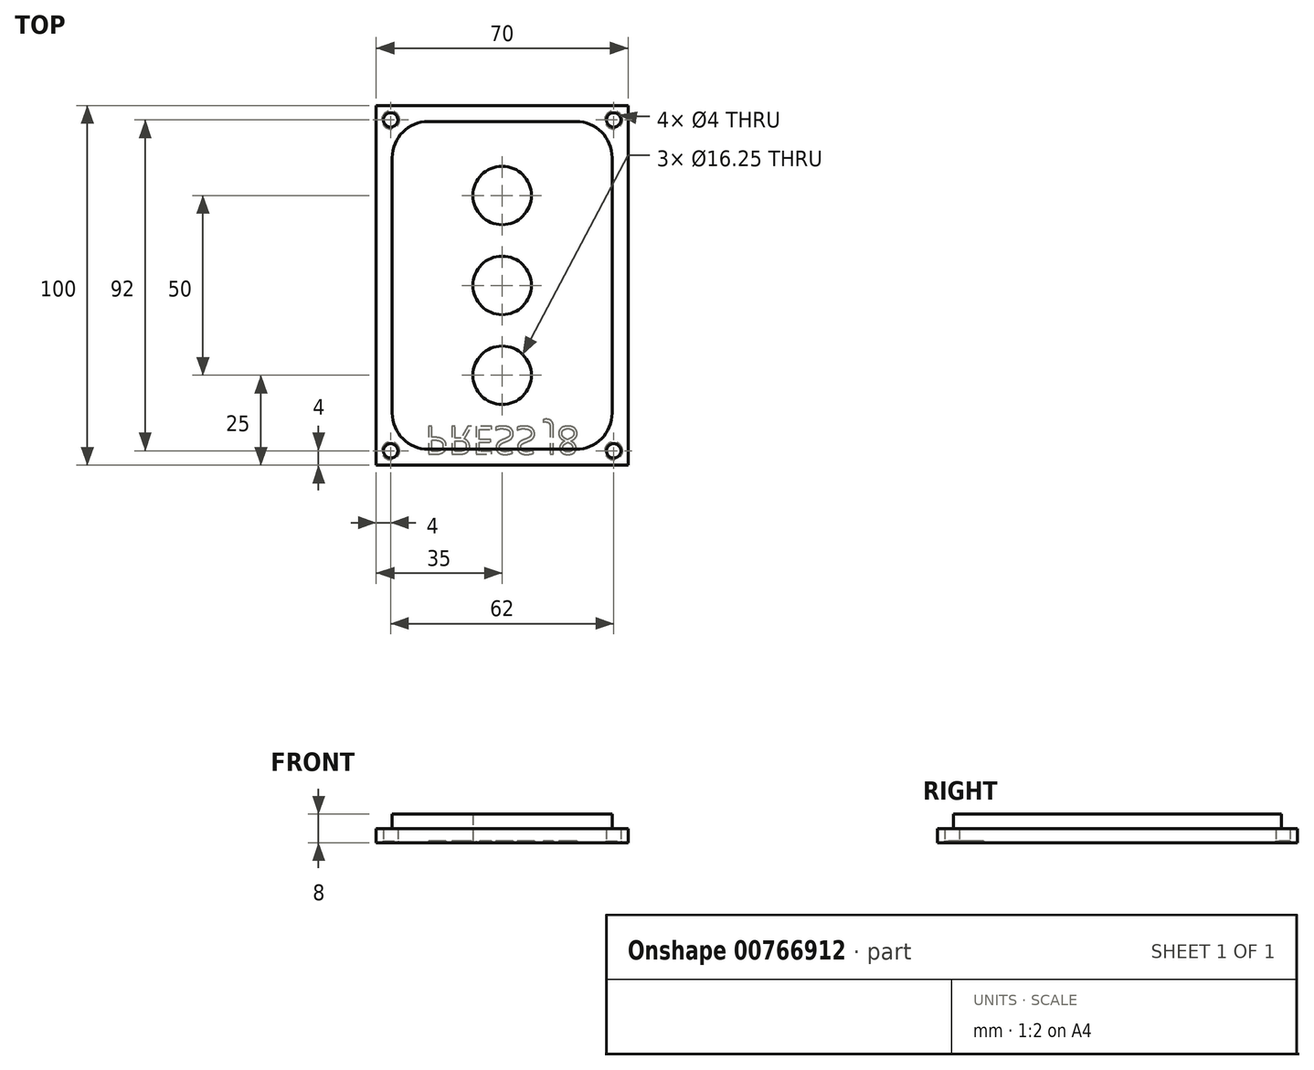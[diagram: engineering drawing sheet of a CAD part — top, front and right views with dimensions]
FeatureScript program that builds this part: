
annotation { "Feature Type Name" : "Feature", "Feature Type Description" : "" }
export const myFeature = defineFeature(function(context is Context, id is Id, definition is map)
    precondition{}
    {
        {
            var Q0;
            Q0=qCreatedBy(makeId("Top.planeOp"),FACE);
            var sketch = newSketch(context, id + "F0", { "sketchPlane" : qUnion([Q0])});
            skLineSegment(sketch, "E0.bottom", {"start": v(-35, 50) * mm, "end": v(35, 50) * mm});
            skLineSegment(sketch, "E0.top", {"start": v(-35, -50) * mm, "end": v(35, -50) * mm});
            skLineSegment(sketch, "E0.left", {"start": v(-35, 50) * mm, "end": v(-35, -50) * mm});
            skLineSegment(sketch, "E0.right", {"start": v(35, 50) * mm, "end": v(35, -50) * mm});
            skSolve(sketch);
        }
        {
            var Q0;
            Q0=qCreatedBy(makeId("Top.planeOp"),FACE);
            var sketch = newSketch(context, id + "F1", { "sketchPlane" : qUnion([Q0])});
            skLineSegment(sketch, "E1.bottom", {"start": v(-30.55, 45.55) * mm, "end": v(30.55, 45.55) * mm});
            skLineSegment(sketch, "E1.top", {"start": v(-30.55, -45.55) * mm, "end": v(30.55, -45.55) * mm});
            skLineSegment(sketch, "E1.left", {"start": v(-30.55, 45.55) * mm, "end": v(-30.55, -45.55) * mm});
            skLineSegment(sketch, "E1.right", {"start": v(30.55, 45.55) * mm, "end": v(30.55, -45.55) * mm});
            skSolve(sketch);
        }
        {
            var Q0;
            Q0=makeQuery(id+"F0.imprint","IMPRINT",FACE,{"disambiguationData":[TD([[makeQuery(id+"F0.imprint","IMPRINT",EDGE,{"derivedFrom":sQuery(id+"F0.wireOp",EDGE,"E0.bottom")}),-1.0]])]});
            extrude(context, id + "F2", {"entities" : qUnion([Q0]), "oppositeDirection" : true, "depth" : 4 * mm, "offsetDistance" : 25 * mm});
        }
        {
            var Q0;
            Q0=makeQuery(id+"F1.imprint","IMPRINT",FACE,{"disambiguationData":[TD([[makeQuery(id+"F1.imprint","IMPRINT",EDGE,{"derivedFrom":sQuery(id+"F1.wireOp",EDGE,"E1.bottom")}),-1.0]])]});
            extrude(context, id + "F3", {"entities" : qUnion([Q0]), "operationType" : NewBodyOperationType.ADD, "depth" : 4 * mm, "offsetDistance" : 25 * mm});
        }
        {
            var Q0;
            Q0=makeQuery(id+"F2.opExtrude","CAP_FACE",FACE,{"disambiguationData":[OSD([sQuery(id+"F0.wireOp",EDGE,"E0.bottom"),sQuery(id+"F0.wireOp",EDGE,"E0.top"),sQuery(id+"F0.wireOp",EDGE,"E0.left"),sQuery(id+"F0.wireOp",EDGE,"E0.right")])],"isStart":false});
            var sketch = newSketch(context, id + "F4", { "sketchPlane" : qUnion([Q0])});
            skPoint(sketch, "E2", {"position": v(0, 25) * mm});
            skPoint(sketch, "E3", {"position": v(0, 0) * mm});
            skPoint(sketch, "E4", {"position": v(0, -25) * mm});
            skSolve(sketch);
        }
        {
            var Q0;
            Q0=sQuery(id+"F4.wireOp",VERTEX,"E2");
            var Q1;
            Q1=sQuery(id+"F4.wireOp",VERTEX,"E3");
            var Q2;
            Q2=sQuery(id+"F4.wireOp",VERTEX,"E4");
            var Q3;
            Q3=makeQuery(id+"F2.opExtrude","SWEPT_BODY",BODY,{"disambiguationData":[OSD([sQuery(id+"F0.wireOp",EDGE,"E0.bottom"),sQuery(id+"F0.wireOp",EDGE,"E0.top"),sQuery(id+"F0.wireOp",EDGE,"E0.left"),sQuery(id+"F0.wireOp",EDGE,"E0.right")])]});
            hole(context, id + "F5", {"style" : HoleStyle.SIMPLE, "endStyle" : HoleEndStyle.BLIND, "holeDiameter" : 16.25 * mm, "majorDiameter" : 5 * mm, "holeDepth" : 10 * mm, "isTappedThrough" : true, "tappedDepth" : 12 * mm, "tapClearance" : 3, "locations" : qUnion([Q0, Q1, Q2]), "scope" : qUnion([Q3])});
        }
        {
            var Q0;
            Q0=makeQuery(id+"F2.opExtrude","CAP_FACE",FACE,{"disambiguationData":[OSD([sQuery(id+"F0.wireOp",EDGE,"E0.bottom"),sQuery(id+"F0.wireOp",EDGE,"E0.top"),sQuery(id+"F0.wireOp",EDGE,"E0.left"),sQuery(id+"F0.wireOp",EDGE,"E0.right")])],"isStart":false});
            var sketch = newSketch(context, id + "F6", { "sketchPlane" : qUnion([Q0])});
            skText(sketch, "E5", { "text": "PRESS J8", "fontName": "OpenSans-Regular.ttf"});
            const initialGuessF6  = {"E5": [-0.0215, 0.03923, 1, 0, 0.00777]};
            skSetInitialGuess(sketch, initialGuessF6);
            skSolve(sketch);
        }
        {
            var Q0;
            Q0 = qSketchRegion(id + "F6", true);
            extrude(context, id + "F7", {"entities" : qUnion([Q0]), "operationType" : NewBodyOperationType.REMOVE, "oppositeDirection" : true, "depth" : .5 * mm, "offsetDistance" : 25 * mm});
        }
        {
            var Q0;
            {var subQ0=sQuery(id+"F0.wireOp",EDGE,"E0.top");var subQ1=sQuery(id+"F0.wireOp",EDGE,"E0.right");var subQ2=sQuery(id+"F0.wireOp",EDGE,"E0.left");var subQ3=sQuery(id+"F0.wireOp",EDGE,"E0.bottom");Q0=makeQuery(id+"F7.boolean.opBoolean","SPLIT",FACE,{"disambiguationData":[TD([makeQuery(id+"F2.opExtrude","SWEPT_FACE",FACE,{"disambiguationData":[OSD([subQ3])]})])],"derivedFrom":makeQuery(id+"F2.opExtrude","CAP_FACE",FACE,{"disambiguationData":[OSD([subQ3,subQ0,subQ2,subQ1])],"isStart":false})});}
            var sketch = newSketch(context, id + "F8", { "sketchPlane" : qUnion([Q0])});
            skPoint(sketch, "E6", {"position": v(-31, 46) * mm});
            skPoint(sketch, "E7", {"position": v(31, 46) * mm});
            skPoint(sketch, "E8", {"position": v(31, -46) * mm});
            skPoint(sketch, "E9", {"position": v(-31, -46) * mm});
            skSolve(sketch);
        }
        {
            var Q0;
            Q0=makeQuery(id+"F3.opExtrude","SWEPT_EDGE",EDGE,{"disambiguationData":[OSD([sQuery(id+"F1.wireOp",EDGE,"E1.top"),sQuery(id+"F1.wireOp",EDGE,"E1.left")])]});
            var Q1;
            Q1=makeQuery(id+"F3.opExtrude","SWEPT_EDGE",EDGE,{"disambiguationData":[OSD([sQuery(id+"F1.wireOp",EDGE,"E1.top"),sQuery(id+"F1.wireOp",EDGE,"E1.right")])]});
            var Q2;
            Q2=makeQuery(id+"F3.opExtrude","SWEPT_EDGE",EDGE,{"disambiguationData":[OSD([sQuery(id+"F1.wireOp",EDGE,"E1.bottom"),sQuery(id+"F1.wireOp",EDGE,"E1.right")])]});
            var Q3;
            Q3=makeQuery(id+"F3.opExtrude","SWEPT_EDGE",EDGE,{"disambiguationData":[OSD([sQuery(id+"F1.wireOp",EDGE,"E1.bottom"),sQuery(id+"F1.wireOp",EDGE,"E1.left")])]});
            fillet(context, id + "F9", {"entities" : qUnion([Q0, Q1, Q2, Q3]), "radius" : 10 * mm, "tangentPropagation" : true, "allowEdgeOverflow" : false});
        }
        {
            var Q0;
            Q0=sQuery(id+"F8.wireOp",VERTEX,"E6");
            var Q1;
            Q1=sQuery(id+"F8.wireOp",VERTEX,"E7");
            var Q2;
            Q2=sQuery(id+"F8.wireOp",VERTEX,"E8");
            var Q3;
            Q3=sQuery(id+"F8.wireOp",VERTEX,"E9");
            var Q4;
            Q4=makeQuery(id+"F2.opExtrude","SWEPT_BODY",BODY,{"disambiguationData":[OSD([sQuery(id+"F0.wireOp",EDGE,"E0.bottom"),sQuery(id+"F0.wireOp",EDGE,"E0.top"),sQuery(id+"F0.wireOp",EDGE,"E0.left"),sQuery(id+"F0.wireOp",EDGE,"E0.right")])]});
            hole(context, id + "F10", {"style" : HoleStyle.C_SINK, "endStyle" : HoleEndStyle.BLIND, "holeDiameter" : 4 * mm, "cSinkDiameter" : 5 * mm, "cSinkAngle" : 90 * degree, "majorDiameter" : 5 * mm, "holeDepth" : 10 * mm, "isTappedThrough" : true, "tappedDepth" : 12 * mm, "tapClearance" : 3, "locations" : qUnion([Q0, Q1, Q2, Q3]), "scope" : qUnion([Q4])});
        }
    });
